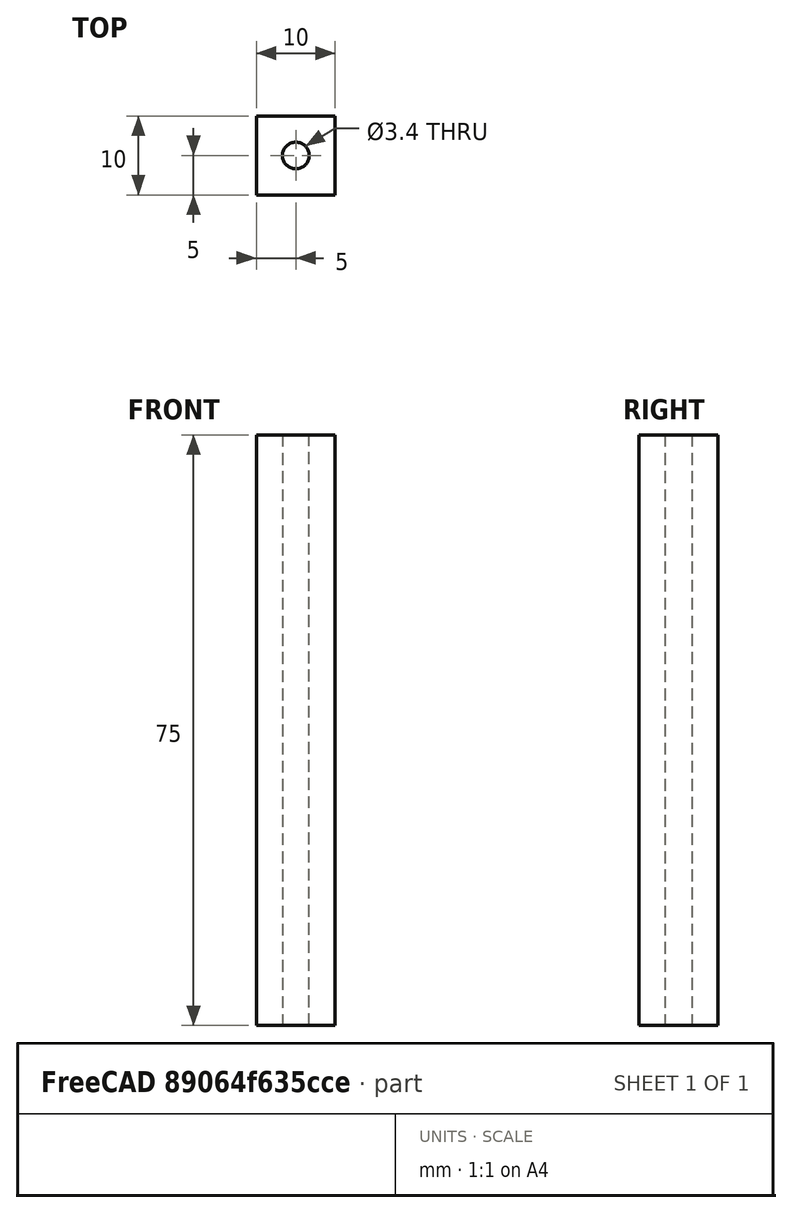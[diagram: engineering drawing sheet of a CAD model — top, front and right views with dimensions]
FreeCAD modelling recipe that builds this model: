
FCSTD DOCUMENT  (FreeCAD 0.18R14555 (Git shallow))
Label: Posts
License: All rights reserved
LicenseURL: http://en.wikipedia.org/wiki/All_rights_reserved
objects: Sketcher::SketchObject×1, PartDesign::Pad×1, PartDesign::Body×1
note: 4 computed .brp shape members not serialized (recipe doc carries the construction recipe); baked Part::Feature solids carry a one-line shape summary decoded from their .brp

FEATURE [Sketcher::SketchObject] Sketch
  MapMode = 5
  Support = -> [XY_Plane]
  sketch-geometry (7):
    g0: LineSegment StartX=0 StartY=10 StartZ=0 EndX=10 EndY=10 EndZ=0
    g1: LineSegment StartX=10 StartY=10 StartZ=0 EndX=10 EndY=0 EndZ=0
    g2: LineSegment StartX=10 StartY=0 StartZ=0 EndX=0 EndY=0 EndZ=0
    g3: LineSegment StartX=0 StartY=0 StartZ=0 EndX=0 EndY=10 EndZ=0
    g4: Circle CenterX=5 CenterY=5 CenterZ=0 NormalX=0 NormalY=0 NormalZ=1 AngleXU=0 Radius=1.7
    g5: LineSegment [constr] StartX=0 StartY=10 StartZ=0 EndX=10 EndY=0 EndZ=0
    g6: LineSegment [constr] StartX=10 StartY=10 StartZ=0 EndX=0 EndY=0 EndZ=0
  constraints (18):
    c: Coincident(g0,g1)
    c: Coincident(g1,g2)
    c: Coincident(g2,g3)
    c: Coincident(g3,g0)
    c: Horizontal(g0)
    c: Horizontal(g2)
    c: Vertical(g1)
    c: Vertical(g3)
    c: Equal(g2,g1)
    c: DistanceX(g2,g2) = 10
    c: Coincident(g2,g-1)
    c: Radius(g4) = 1.7
    c: Coincident(g5,g0)
    c: Coincident(g6,g0)
    c: Coincident(g6,g2)
    c: Coincident(g5,g1)
    c: PointOnObject(g4,g5)
    c: PointOnObject(g4,g6)
FEATURE [PartDesign::Pad] Pad
  Length = 75
  Length2 = 100
  Profile = -> Sketch
  Type = 0
FEATURE [PartDesign::Body] Body
  Group = -> [Sketch,Pad]
  Origin = -> Origin
  Tip = -> Pad
